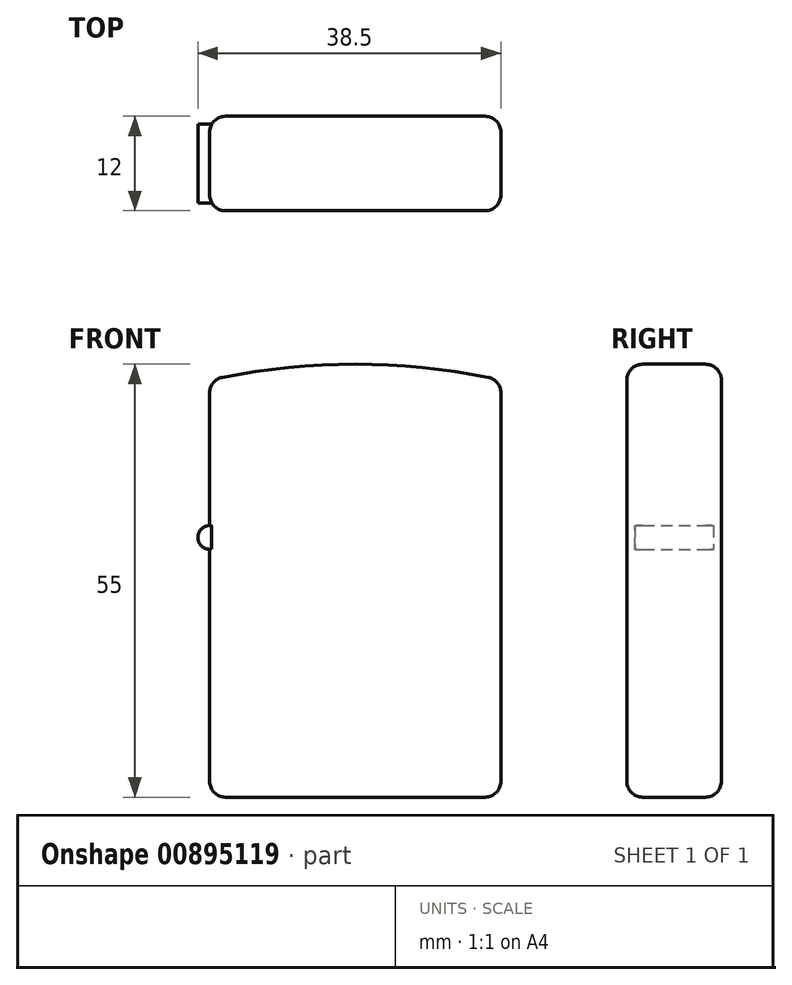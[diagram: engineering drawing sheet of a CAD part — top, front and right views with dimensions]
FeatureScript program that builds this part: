
annotation { "Feature Type Name" : "Feature", "Feature Type Description" : "" }
export const myFeature = defineFeature(function(context is Context, id is Id, definition is map)
    precondition{}
    {
        {
            var Q0;
            Q0=qCreatedBy(makeId("Front.planeOp"),FACE);
            var sketch = newSketch(context, id + "F0", { "sketchPlane" : qUnion([Q0])});
            skLineSegment(sketch, "E0.bottom", {"start": v(0, 0) * mm, "end": v(37, 0) * mm});
            skLineSegment(sketch, "E0.top", {"start": v(0, 53) * mm, "end": v(37, 53) * mm});
            skLineSegment(sketch, "E0.left", {"start": v(0, 0) * mm, "end": v(0, 53) * mm});
            skLineSegment(sketch, "E0.right", {"start": v(37, 0) * mm, "end": v(37, 53) * mm});
            skArc(sketch, "E1", {"start": v(37, 53) * mm, "mid": v(18.5, 55) * mm, "end": v(0, 53) * mm});
            skSolve(sketch);
        }
        {
            var Q0;
            Q0 = qSketchRegion(id + "F0", true);
            extrude(context, id + "F1", {"entities" : qUnion([Q0]), "depth" : 12 * mm, "offsetDistance" : 25.4 * mm});
        }
        {
            var Q0;
            Q0=makeQuery(id+"F1.opExtrude","SWEPT_EDGE",EDGE,{"disambiguationData":[OSD([sQuery(id+"F0.wireOp",EDGE,"E0.top"),sQuery(id+"F0.wireOp",EDGE,"E0.right"),sQuery(id+"F0.wireOp",EDGE,"E1")])]});
            var Q1;
            Q1=makeQuery(id+"F1.opExtrude","CAP_EDGE",EDGE,{"disambiguationData":[OSD([sQuery(id+"F0.wireOp",EDGE,"E1")])],"isStart":false});
            var Q2;
            Q2=makeQuery(id+"F1.opExtrude","SWEPT_EDGE",EDGE,{"disambiguationData":[OSD([sQuery(id+"F0.wireOp",EDGE,"E0.top"),sQuery(id+"F0.wireOp",EDGE,"E0.left"),sQuery(id+"F0.wireOp",EDGE,"E1")])]});
            var Q3;
            Q3=makeQuery(id+"F1.opExtrude","CAP_EDGE",EDGE,{"disambiguationData":[OSD([sQuery(id+"F0.wireOp",EDGE,"E1")])],"isStart":true});
            var Q4;
            Q4=makeQuery(id+"F1.opExtrude","CAP_EDGE",EDGE,{"disambiguationData":[OSD([sQuery(id+"F0.wireOp",EDGE,"E0.right")])],"isStart":false});
            var Q5;
            Q5=makeQuery(id+"F1.opExtrude","CAP_EDGE",EDGE,{"disambiguationData":[OSD([sQuery(id+"F0.wireOp",EDGE,"E0.right")])],"isStart":true});
            var Q6;
            Q6=makeQuery(id+"F1.opExtrude","SWEPT_EDGE",EDGE,{"disambiguationData":[OSD([sQuery(id+"F0.wireOp",EDGE,"E0.bottom"),sQuery(id+"F0.wireOp",EDGE,"E0.right")])]});
            var Q7;
            Q7=makeQuery(id+"F1.opExtrude","CAP_EDGE",EDGE,{"disambiguationData":[OSD([sQuery(id+"F0.wireOp",EDGE,"E0.bottom")])],"isStart":false});
            var Q8;
            Q8=makeQuery(id+"F1.opExtrude","CAP_EDGE",EDGE,{"disambiguationData":[OSD([sQuery(id+"F0.wireOp",EDGE,"E0.left")])],"isStart":false});
            var Q9;
            Q9=makeQuery(id+"F1.opExtrude","CAP_EDGE",EDGE,{"disambiguationData":[OSD([sQuery(id+"F0.wireOp",EDGE,"E0.left")])],"isStart":true});
            var Q10;
            Q10=makeQuery(id+"F1.opExtrude","CAP_EDGE",EDGE,{"disambiguationData":[OSD([sQuery(id+"F0.wireOp",EDGE,"E0.bottom")])],"isStart":true});
            var Q11;
            Q11=makeQuery(id+"F1.opExtrude","SWEPT_EDGE",EDGE,{"disambiguationData":[OSD([sQuery(id+"F0.wireOp",EDGE,"E0.bottom"),sQuery(id+"F0.wireOp",EDGE,"E0.left")])]});
            fillet(context, id + "F2", {"entities" : qUnion([Q0, Q1, Q2, Q3, Q4, Q5, Q6, Q7, Q8, Q9, Q10, Q11]), "radius" : 2 * mm, "tangentPropagation" : true, "allowEdgeOverflow" : false});
        }
        {
            var Q0;
            Q0=qCreatedBy(makeId("Front.planeOp"),FACE);
            cPlane(context, id + "F3", {"entities" : qUnion([Q0]), "cplaneType" : CPlaneType.OFFSET, "offset" : 6 * mm, "width" : 152.4 * mm, "height" : 152.4 * mm});
        }
        {
            var Q0;
            Q0=qCreatedBy(id+"F3.planeOp",FACE);
            var sketch = newSketch(context, id + "F4", { "sketchPlane" : qUnion([Q0])});
            skCircle(sketch, "E2", {"center": v(0, 33) * mm, "radius": 1.5 * mm});
            skSolve(sketch);
        }
        {
            var Q0;
            Q0 = qSketchRegion(id + "F4", true);
            extrude(context, id + "F5", {"entities" : qUnion([Q0]), "operationType" : NewBodyOperationType.ADD, "endBound" : BoundingType.SYMMETRIC, "depth" : 10 * mm, "offsetDistance" : 25.4 * mm});
        }
    });
